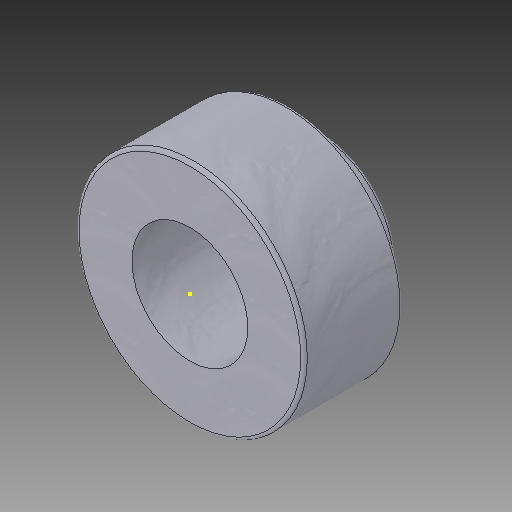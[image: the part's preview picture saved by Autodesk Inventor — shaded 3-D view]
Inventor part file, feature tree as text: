
AUTODESK INVENTOR PART (.ipt)
format: ipt  version: 2019 (Build 230136000, 136)  size: 204,288 bytes
history: native  units: in
note: dims shown in document units (in); Inventor stores cm internally (conversion verified against a paired STEP export)
features: sketch x6, other x3
ambient origin geometry x8: Origin, YZ Plane, XZ Plane, XY Plane, X Axis, Y Axis, Z Axis, Center Point
bodies: Solid1 (feature_tree)
feature tree (9):
  other  "project flange bearing part2.ipt"
  other  "Solid1::project flange bearing part2.ipt"
  other  "TaggingFeature1"
  sketch  "Sketch1"  dims[d0=0.3937in]
  sketch  "Sketch2"
  sketch  "Sketch3"
  sketch  "Sketch4"
  sketch  "Sketch5"
  sketch  "Sketch6"
